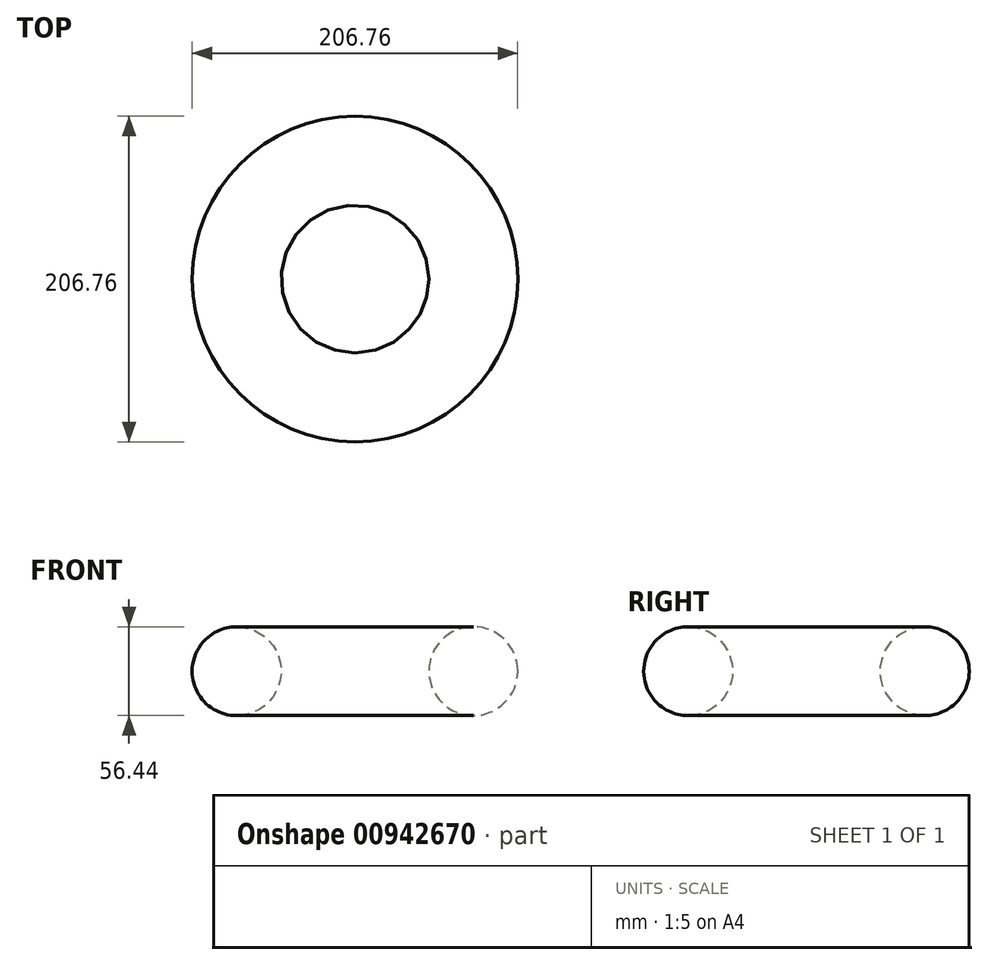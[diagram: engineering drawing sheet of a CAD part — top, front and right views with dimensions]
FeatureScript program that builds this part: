
annotation { "Feature Type Name" : "Feature", "Feature Type Description" : "" }
export const myFeature = defineFeature(function(context is Context, id is Id, definition is map)
    precondition{}
    {
        {
            var Q0;
            Q0=qCreatedBy(makeId("Front.planeOp"),FACE);
            var sketch = newSketch(context, id + "F0", { "sketchPlane" : qUnion([Q0])});
            skLineSegment(sketch, "E0", {"start": v(0, 110.15) * mm, "end": v(0, -104.81) * mm, "construction": true});
            skCircle(sketch, "E1", {"center": v(75.16, 0) * mm, "radius": 28.22 * mm});
            skSolve(sketch);
        }
        {
            var Q0;
            Q0 = qSketchRegion(id + "F0", true);
            var Q1;
            Q1=sQuery(id+"F0.wireOp",EDGE,"E0");
            revolve(context, id + "F1", {"surfaceOperationType" : NewSurfaceOperationType.NEW, "entities" : qUnion([Q0]), "axis" : qUnion([Q1]), "revolveType" : RevolveType.FULL});
        }
    });
